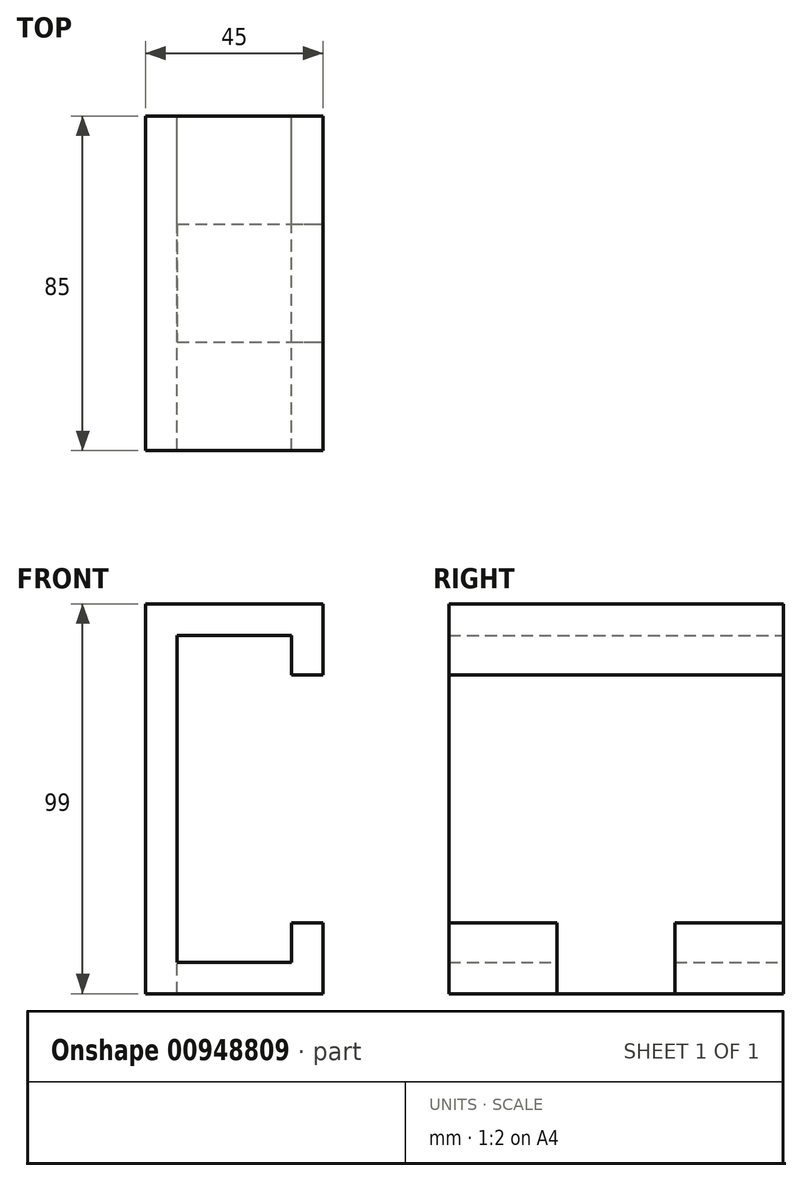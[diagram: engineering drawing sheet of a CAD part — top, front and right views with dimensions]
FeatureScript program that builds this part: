
annotation { "Feature Type Name" : "Feature", "Feature Type Description" : "" }
export const myFeature = defineFeature(function(context is Context, id is Id, definition is map)
    precondition{}
    {
        {
            var Q0;
            Q0=qCreatedBy(makeId("Front.planeOp"),FACE);
            var sketch = newSketch(context, id + "F0", { "sketchPlane" : qUnion([Q0])});
            skLineSegment(sketch, "E0", {"start": v(0, 0) * mm, "end": v(0, 41.5) * mm});
            skLineSegment(sketch, "E1", {"start": v(0, 41.5) * mm, "end": v(29, 41.5) * mm});
            skLineSegment(sketch, "E2.MirrorCS", {"start": v(0, 0) * mm, "end": v(0, -41.5) * mm});
            skLineSegment(sketch, "E3.MirrorCS", {"start": v(0, -41.5) * mm, "end": v(29, -41.5) * mm});
            skLineSegment(sketch, "E4", {"start": v(29, 41.5) * mm, "end": v(29, 31.5) * mm});
            skLineSegment(sketch, "E5.MirrorCS", {"start": v(29, -41.5) * mm, "end": v(29, -31.5) * mm});
            skLineSegment(sketch, "E6.0", {"start": v(37, 49.5) * mm, "end": v(37, 31.5) * mm});
            skLineSegment(sketch, "E6.1", {"start": v(-8, 49.5) * mm, "end": v(37, 49.5) * mm});
            skLineSegment(sketch, "E6.2", {"start": v(37, -49.5) * mm, "end": v(37, -31.5) * mm});
            skLineSegment(sketch, "E6.3", {"start": v(-8, -49.5) * mm, "end": v(37, -49.5) * mm});
            skLineSegment(sketch, "E6.4", {"start": v(-8, 0) * mm, "end": v(-8, -49.5) * mm});
            skLineSegment(sketch, "E6.5", {"start": v(-8, 0) * mm, "end": v(-8, 49.5) * mm});
            skLineSegment(sketch, "E7", {"start": v(29, 31.5) * mm, "end": v(37, 31.5) * mm});
            skLineSegment(sketch, "E8", {"start": v(29, -31.5) * mm, "end": v(37, -31.5) * mm});
            skSolve(sketch);
        }
        {
            var Q0;
            Q0 = qSketchRegion(id + "F0", true);
            extrude(context, id + "F1", {"entities" : qUnion([Q0]), "depth" : 85 * mm, "offsetDistance" : 25 * mm, "symmetric" : true});
        }
        {
            var Q0;
            Q0=makeQuery(id+"F1.opExtrude","SWEPT_FACE",FACE,{"disambiguationData":[OSD([sQuery(id+"F0.wireOp",EDGE,"E6.2")])]});
            var sketch = newSketch(context, id + "F2", { "sketchPlane" : qUnion([Q0])});
            skLineSegment(sketch, "E9.bottom", {"start": v(15, -31.5) * mm, "end": v(-15, -31.5) * mm});
            skLineSegment(sketch, "E9.top", {"start": v(15, -49.5) * mm, "end": v(-15, -49.5) * mm});
            skLineSegment(sketch, "E9.left", {"start": v(15, -31.5) * mm, "end": v(15, -49.5) * mm});
            skLineSegment(sketch, "E9.right", {"start": v(-15, -31.5) * mm, "end": v(-15, -49.5) * mm});
            skPoint(sketch, "E9.middle", {"position": v(0, -40.5) * mm});
            skSolve(sketch);
        }
        {
            var Q0;
            Q0 = qSketchRegion(id + "F2", true);
            var Q1;
            Q1=makeQuery(id+"F1.opExtrude","SWEPT_FACE",FACE,{"disambiguationData":[OSD([sQuery(id+"F0.wireOp",EDGE,"E0"),sQuery(id+"F0.wireOp",EDGE,"E2.MirrorCS")])]});
            extrude(context, id + "F3", {"entities" : qUnion([Q0]), "operationType" : NewBodyOperationType.REMOVE, "endBound" : BoundingType.UP_TO_SURFACE, "oppositeDirection" : true, "depth" : 25 * mm, "endBoundEntityFace" : qUnion([Q1]), "offsetDistance" : 25 * mm});
        }
    });
